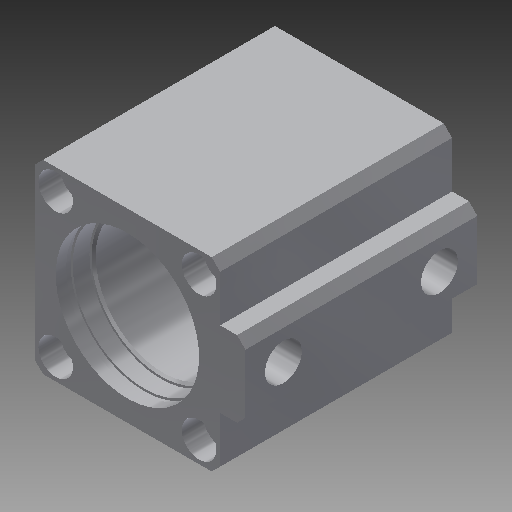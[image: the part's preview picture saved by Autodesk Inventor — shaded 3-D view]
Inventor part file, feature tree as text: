
AUTODESK INVENTOR PART (.ipt)
format: ipt  version: 2017 SP1 (Build 210196100, 196)  size: 280,064 bytes
history: native  units: mm
features: sketch x10, extrude x9, chamfer x2, plane x2, hole x2, mirror x1, projected_geometry x1
ambient origin geometry x8: Origin, YZ Plane, XZ Plane, XY Plane, X Axis, Y Axis, Z Axis, Center Point
bodies: Solid1 (feature_tree)
feature tree (27):
  extrude  "Extrusion1"  Depth=44.0mm
  extrude  "Extrusion2"  Depth=6.0mm
  extrude  "Extrusion3"  Depth=55.0mm
  chamfer  "Chamfer1"  Distance=55.0mm
  plane  "Work Plane1"
  extrude  "Extrusion4"  Depth=47.0mm TaperAngle=0.0deg
  extrude  "Extrusion5"  Depth=8.0mm TaperAngle=0.0deg
  extrude  "Extrusion6"  [1 undecoded]
  extrude  "Extrusion7"  Depth=1.5mm TaperAngle=0.0deg
  extrude  "Extrusion8"  Depth=50.0mm
  chamfer  "Chamfer2"  Distance=1.5mm
  extrude  "Extrusion9"  Depth=9.0mm
  plane  "Work Plane2"
  mirror  "Mirror1"
  hole  "Hole2"  [1 undecoded]
  sketch  "Sketch1"  dims[d0=44.0mm d1=44.0mm]
  sketch  "Sketch2"  dims[d2=12.0mm d3=6.0mm]
  sketch  "Sketch3"  dims[d4=34.0mm d5=34.0mm d6=55.0mm d7=0.0mm]
  sketch  "Sketch4"  dims[d8=32.0mm d9=47.0mm d10=0.0mm]
  projected_geometry  "Projected Loop1"
  sketch  "Sketch5"  dims[d11=34.0mm d12=8.0mm d13=0.0mm]
  sketch  "Sketch6"  dims[d14=0.5mm d15=2.0mm d16=45.0deg d17=-4.0mm]
  sketch  "Sketch7"  dims[d18=35.0mm d19=1.5mm d20=0.0mm]
  sketch  "Sketch8"  dims[d21=18.0mm d22=50.0mm d23=1.5mm d24=0.0mm]
  sketch  "Sketch9"  dims[d25=8.75mm d26=9.0mm]
  sketch  "Sketch10"  dims[d27=9.0mm d28=0.0mm d29=46.0mm d30=9.0mm d31=0.0mm d32=3.0mm d33=9.0mm d34=0.0mm d35=2.0mm d36=2.0mm d37=45.0deg d38=8.2mm d39=5.2mm d40=0.0mm d41=4.917mm d42=12.8mm d43=4.0mm d44=2.0mm d45=90.0deg d46=15.8mm d47=120.0deg]
  hole  "Hole1"  [1 undecoded]
note: 3 required parameter values undecoded (feature->parameter linkage not recoverable at this tier; creation-order binding heuristic only, values carry confidence <= 0.55)
